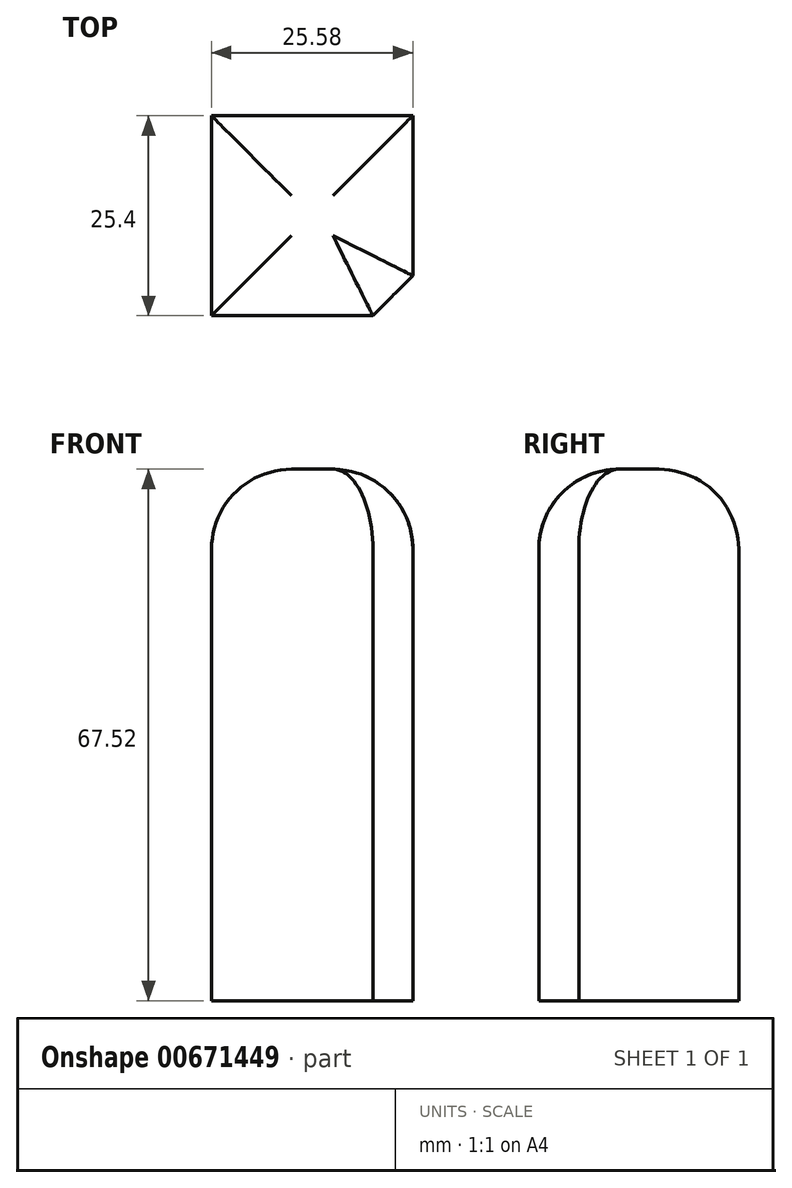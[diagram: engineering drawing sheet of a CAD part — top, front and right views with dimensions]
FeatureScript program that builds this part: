
annotation { "Feature Type Name" : "Feature", "Feature Type Description" : "" }
export const myFeature = defineFeature(function(context is Context, id is Id, definition is map)
    precondition{}
    {
        {
            var Q0;
            Q0=qCreatedBy(makeId("Front.planeOp"),FACE);
            var sketch = newSketch(context, id + "F0", { "sketchPlane" : qUnion([Q0])});
            skLineSegment(sketch, "E0.bottom", {"start": v(0, 0) * mm, "end": v(0, 0) * mm});
            skLineSegment(sketch, "E0.top", {"start": v(0, 17.72) * mm, "end": v(0, 17.72) * mm});
            skLineSegment(sketch, "E0.left", {"start": v(0, 0) * mm, "end": v(0, 17.72) * mm});
            skLineSegment(sketch, "E0.right", {"start": v(0, 0) * mm, "end": v(0, 17.72) * mm});
            skLineSegment(sketch, "E1.bottom", {"start": v(-46.94, 0) * mm, "end": v(0, 0) * mm});
            skLineSegment(sketch, "E1.top", {"start": v(-46.94, 17.72) * mm, "end": v(0, 17.72) * mm});
            skLineSegment(sketch, "E1.left", {"start": v(-46.94, 0) * mm, "end": v(-46.94, 17.72) * mm});
            skLineSegment(sketch, "E2.bottom", {"start": v(-6.44, 17.72) * mm, "end": v(-14.29, 17.72) * mm});
            skLineSegment(sketch, "E2.top", {"start": v(-6.44, -24.59) * mm, "end": v(-14.29, -24.59) * mm});
            skLineSegment(sketch, "E2.left", {"start": v(-6.44, 17.72) * mm, "end": v(-6.44, -24.59) * mm});
            skLineSegment(sketch, "E2.right", {"start": v(-14.29, 17.72) * mm, "end": v(-14.29, -24.59) * mm});
            skLineSegment(sketch, "E3.bottom", {"start": v(0, -24.59) * mm, "end": v(25.58, -24.59) * mm});
            skLineSegment(sketch, "E3.top", {"start": v(0, 42.93) * mm, "end": v(25.58, 42.93) * mm});
            skLineSegment(sketch, "E3.left", {"start": v(0, -24.59) * mm, "end": v(0, 42.93) * mm});
            skLineSegment(sketch, "E3.right", {"start": v(25.58, -24.59) * mm, "end": v(25.58, 42.93) * mm});
            skSolve(sketch);
        }
        {
            var Q0;
            {var subQ3=sQuery(id+"F0.wireOp",EDGE,"E3.bottom");Q0=makeQuery(id+"F0.imprint","IMPRINT",FACE,{"disambiguationData":[TD([[makeQuery(id+"F0.imprint","IMPRINT",EDGE,{"derivedFrom":subQ3}),1.0]])]});}
            extrude(context, id + "F1", {"entities" : qUnion([Q0]), "depth" : 25.4 * mm, "offsetDistance" : 25.4 * mm});
        }
        {
            var Q0;
            Q0=makeQuery(id+"F1.opExtrude","CAP_EDGE",EDGE,{"disambiguationData":[OSD([sQuery(id+"F0.wireOp",EDGE,"E3.top")])],"isStart":false});
            var Q1;
            Q1=makeQuery(id+"F1.opExtrude","SWEPT_EDGE",EDGE,{"disambiguationData":[OSD([sQuery(id+"F0.wireOp",EDGE,"E3.top"),sQuery(id+"F0.wireOp",EDGE,"E3.right")])]});
            var Q2;
            Q2=makeQuery(id+"F1.opExtrude","CAP_EDGE",EDGE,{"disambiguationData":[OSD([sQuery(id+"F0.wireOp",EDGE,"E3.top")])],"isStart":true});
            var Q3;
            Q3=makeQuery(id+"F1.opExtrude","SWEPT_EDGE",EDGE,{"disambiguationData":[OSD([sQuery(id+"F0.wireOp",EDGE,"E3.top"),sQuery(id+"F0.wireOp",EDGE,"E3.left")])]});
            fillet(context, id + "F2", {"entities" : qUnion([Q0, Q1, Q2, Q3]), "radius" : 10.16 * mm, "tangentPropagation" : true, "allowEdgeOverflow" : false});
        }
        {
            var Q0;
            Q0=makeQuery(id+"F1.opExtrude","CAP_EDGE",EDGE,{"disambiguationData":[OSD([sQuery(id+"F0.wireOp",EDGE,"E3.right")])],"isStart":false});
            chamfer(context, id + "F3", {"entities" : qUnion([Q0]), "width" : 5.08 * mm, "tangentPropagation" : true});
        }
    });
